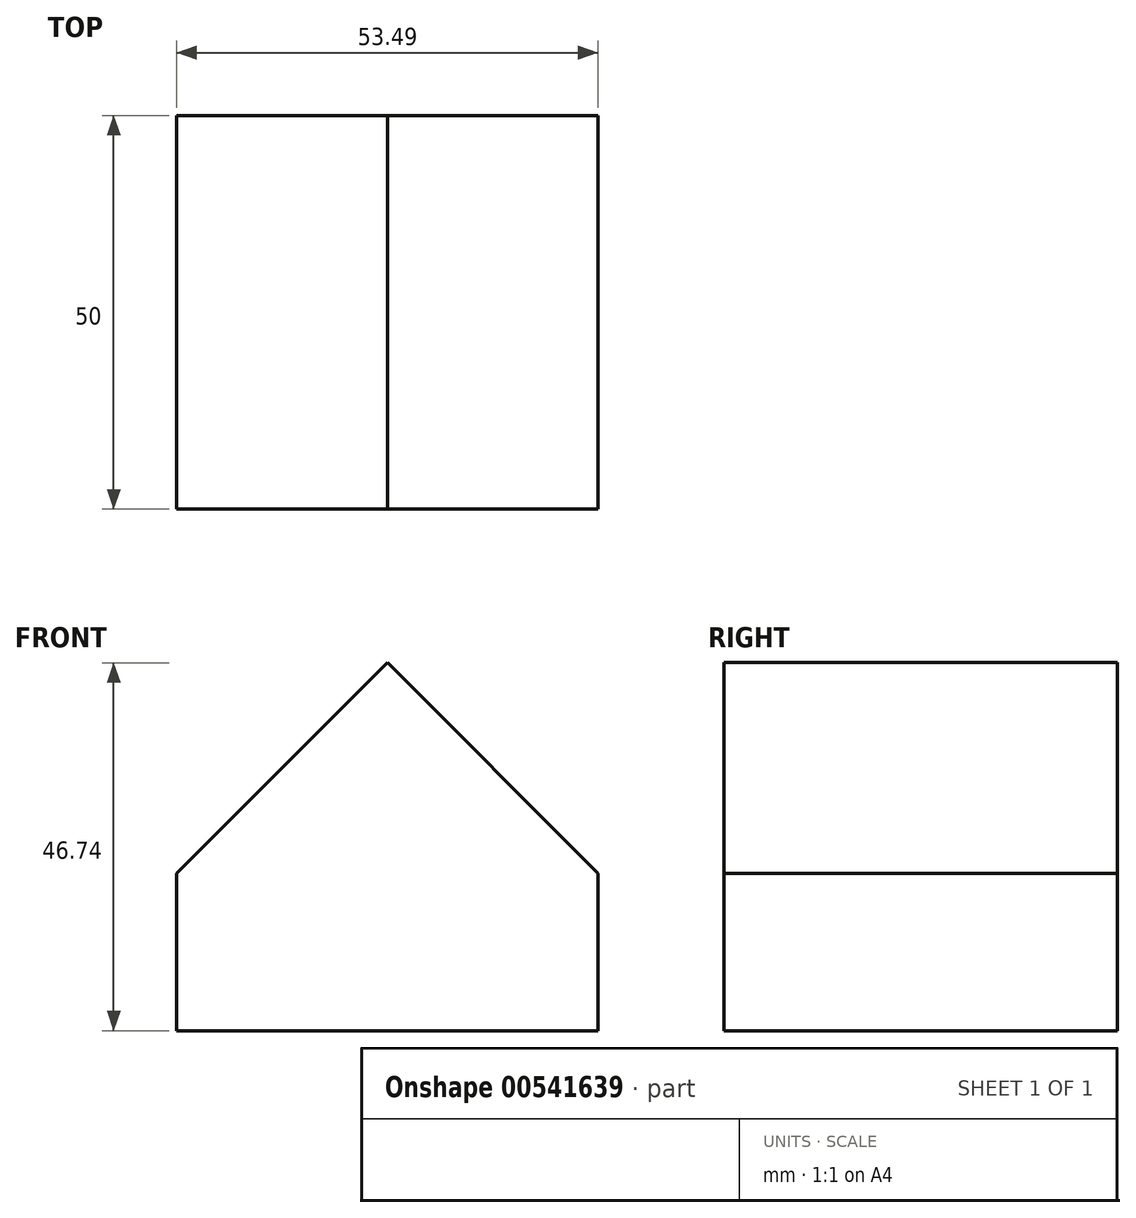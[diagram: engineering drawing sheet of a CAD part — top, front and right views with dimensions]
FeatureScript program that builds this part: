
annotation { "Feature Type Name" : "Feature", "Feature Type Description" : "" }
export const myFeature = defineFeature(function(context is Context, id is Id, definition is map)
    precondition{}
    {
        {
            var Q0;
            Q0=qCreatedBy(makeId("Front.planeOp"),FACE);
            var sketch = newSketch(context, id + "F0", { "sketchPlane" : qUnion([Q0])});
            skLineSegment(sketch, "E0.bottom", {"start": v(0, 0) * mm, "end": v(53.49, 0) * mm});
            skLineSegment(sketch, "E0.top", {"start": v(0, 50) * mm, "end": v(53.49, 50) * mm});
            skLineSegment(sketch, "E0.left", {"start": v(0, 0) * mm, "end": v(0, 50) * mm});
            skLineSegment(sketch, "E0.right", {"start": v(53.49, 0) * mm, "end": v(53.49, 50) * mm});
            skSolve(sketch);
        }
        {
            var Q0;
            Q0=makeQuery(id+"F0.imprint","IMPRINT",FACE,{"disambiguationData":[TD([[makeQuery(id+"F0.imprint","IMPRINT",EDGE,{"derivedFrom":sQuery(id+"F0.wireOp",EDGE,"E0.bottom")}),1.0]])]});
            extrude(context, id + "F1", {"entities" : qUnion([Q0]), "depth" : 50 * mm, "offsetDistance" : 25 * mm});
        }
        {
            var Q0;
            Q0=makeQuery(id+"F1.opExtrude","SWEPT_EDGE",EDGE,{"disambiguationData":[OSD([sQuery(id+"F0.wireOp",EDGE,"E0.top"),sQuery(id+"F0.wireOp",EDGE,"E0.right")])]});
            var Q1;
            Q1=makeQuery(id+"F1.opExtrude","SWEPT_EDGE",EDGE,{"disambiguationData":[OSD([sQuery(id+"F0.wireOp",EDGE,"E0.top"),sQuery(id+"F0.wireOp",EDGE,"E0.left")])]});
            chamfer(context, id + "F2", {"entities" : qUnion([Q0, Q1]), "width" : 30 * mm, "tangentPropagation" : true});
        }
    });
